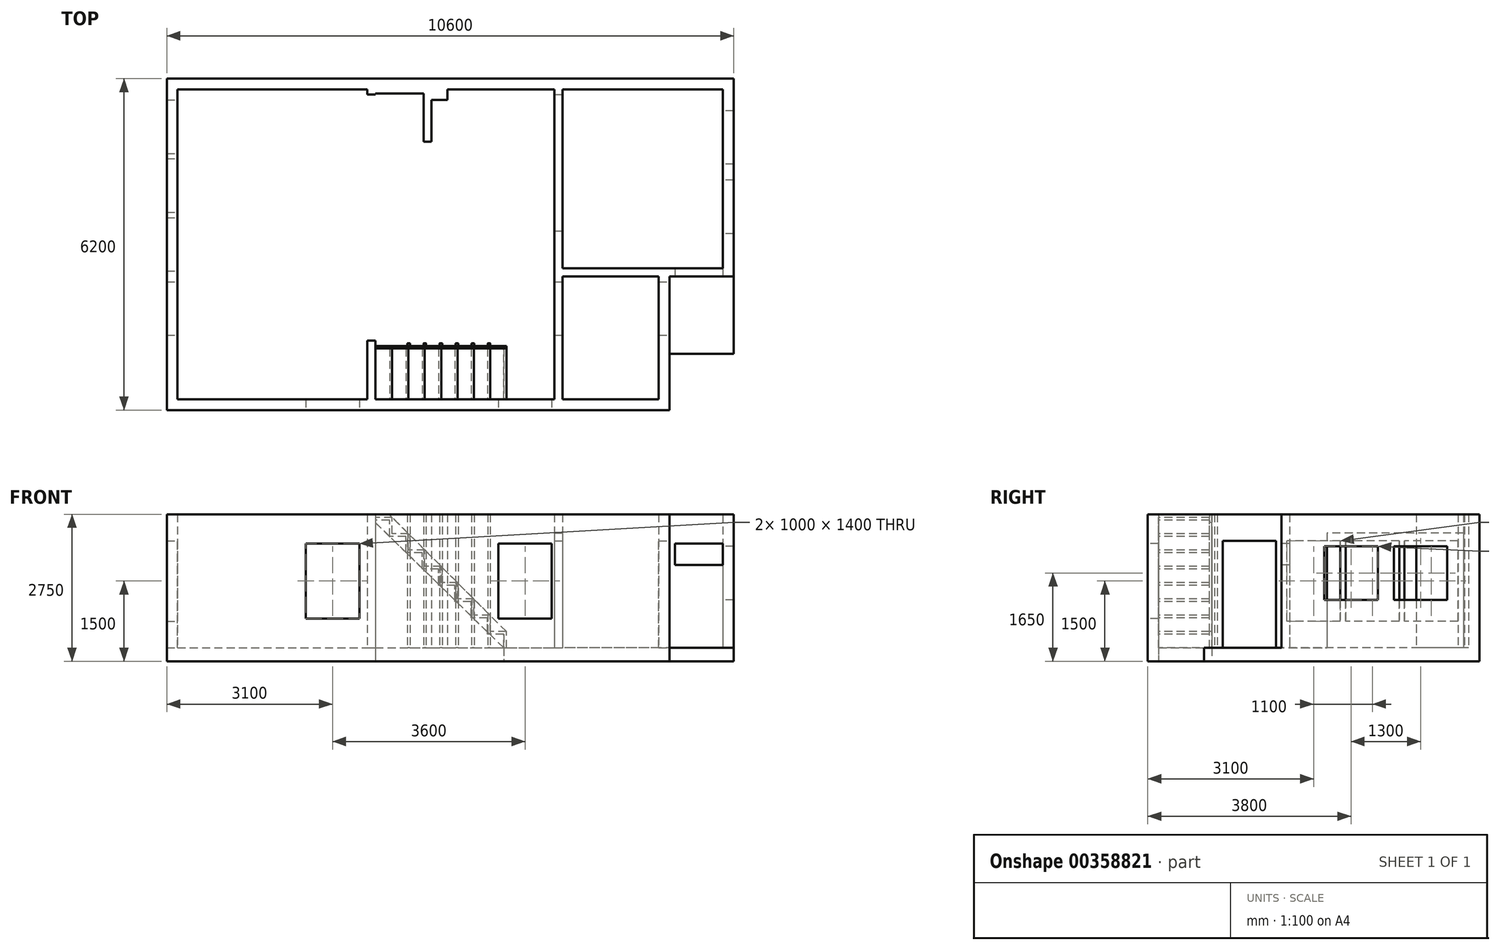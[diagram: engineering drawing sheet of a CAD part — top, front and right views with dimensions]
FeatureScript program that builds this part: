
annotation { "Feature Type Name" : "Feature", "Feature Type Description" : "" }
export const myFeature = defineFeature(function(context is Context, id is Id, definition is map)
    precondition{}
    {
        {
            var Q0;
            Q0=qCreatedBy(makeId("Top.planeOp"),FACE);
            var sketch = newSketch(context, id + "F0", { "sketchPlane" : qUnion([Q0])});
            skLineSegment(sketch, "E0.bottom", {"start": v(0, 0) * mm, "end": v(10600, 0) * mm});
            skLineSegment(sketch, "E0.top", {"start": v(0, -6200) * mm, "end": v(9400, -6200) * mm});
            skLineSegment(sketch, "E0.left", {"start": v(0, 0) * mm, "end": v(0, -6200) * mm});
            skLineSegment(sketch, "E0.right", {"start": v(10600, 0) * mm, "end": v(10600, -5150) * mm});
            skLineSegment(sketch, "E1.top", {"start": v(10600, -5150) * mm, "end": v(9400, -5150) * mm});
            skLineSegment(sketch, "E1.right", {"start": v(9400, -6200) * mm, "end": v(9400, -5150) * mm});
            skLineSegment(sketch, "E2.top", {"start": v(3900, -5000) * mm, "end": v(6300, -5000) * mm});
            skLineSegment(sketch, "E2.left", {"start": v(3900, -6000) * mm, "end": v(3900, -5000) * mm});
            skLineSegment(sketch, "E2.right", {"start": v(6300, -6000) * mm, "end": v(6300, -5000) * mm});
            skLineSegment(sketch, "E3.top", {"start": v(3900, -6000) * mm, "end": v(6300, -6000) * mm});
            skSolve(sketch);
        }
        {
            var Q0;
            Q0 = qSketchRegion(id + "F0", true);
            extrude(context, id + "F1", {"entities" : qUnion([Q0]), "depth" : 250 * mm});
        }
        {
            var Q0;
            Q0=makeQuery(id+"F1.opExtrude","CAP_FACE",FACE,{"disambiguationData":[OSD([sQuery(id+"F0.wireOp",EDGE,"E0.bottom"),sQuery(id+"F0.wireOp",EDGE,"E0.top"),sQuery(id+"F0.wireOp",EDGE,"E0.left"),sQuery(id+"F0.wireOp",EDGE,"E0.right")])],"isStart":false});
            var sketch = newSketch(context, id + "F2", { "sketchPlane" : qUnion([Q0])});
            skLineSegment(sketch, "E4.bottom", {"start": v(200, -200) * mm, "end": v(3750, -200) * mm});
            skLineSegment(sketch, "E4.top", {"start": v(200, -6000) * mm, "end": v(3750, -6000) * mm});
            skLineSegment(sketch, "E4.left", {"start": v(200, -200) * mm, "end": v(200, -6000) * mm});
            skLineSegment(sketch, "E4.right", {"start": v(10400, -200) * mm, "end": v(10400, -3550) * mm});
            skLineSegment(sketch, "E5.bottom", {"start": v(9200, -6000) * mm, "end": v(7400, -6000) * mm});
            skLineSegment(sketch, "E5.top", {"start": v(10400, -3550) * mm, "end": v(7400, -3550) * mm});
            skLineSegment(sketch, "E6.top", {"start": v(3750, -4900) * mm, "end": v(3900, -4900) * mm});
            skLineSegment(sketch, "E6.left", {"start": v(3750, -6000) * mm, "end": v(3750, -4900) * mm});
            skLineSegment(sketch, "E6.right", {"start": v(3900, -6000) * mm, "end": v(3900, -4900) * mm});
            skLineSegment(sketch, "E7.top", {"start": v(3750, -300) * mm, "end": v(3900, -300) * mm});
            skLineSegment(sketch, "E7.left", {"start": v(3750, -200) * mm, "end": v(3750, -300) * mm});
            skLineSegment(sketch, "E7.right", {"start": v(3900, -280) * mm, "end": v(3900, -300) * mm});
            skLineSegment(sketch, "E8.top", {"start": v(4800, -1180) * mm, "end": v(4950, -1180) * mm});
            skLineSegment(sketch, "E8.left", {"start": v(4800, -280) * mm, "end": v(4800, -1180) * mm});
            skLineSegment(sketch, "E8.right", {"start": v(4950, -400) * mm, "end": v(4950, -1180) * mm});
            skLineSegment(sketch, "E9.top", {"start": v(7250, -300) * mm, "end": v(7400, -300) * mm});
            skLineSegment(sketch, "E9.left", {"start": v(7250, -200) * mm, "end": v(7250, -300) * mm});
            skLineSegment(sketch, "E9.right", {"start": v(7400, -200) * mm, "end": v(7400, -300) * mm});
            skLineSegment(sketch, "E10.top", {"start": v(9200, -3700) * mm, "end": v(7400, -3700) * mm});
            skLineSegment(sketch, "E10.right", {"start": v(7400, -6000) * mm, "end": v(7400, -3700) * mm});
            skLineSegment(sketch, "E11.top", {"start": v(7250, -2850) * mm, "end": v(7400, -2850) * mm});
            skLineSegment(sketch, "E11.left", {"start": v(7250, -6000) * mm, "end": v(7250, -2850) * mm});
            skLineSegment(sketch, "E11.right", {"start": v(7400, -3550) * mm, "end": v(7400, -2850) * mm});
            skLineSegment(sketch, "E12.bottom", {"start": v(0, 0) * mm, "end": v(10600, 0) * mm});
            skLineSegment(sketch, "E12.top", {"start": v(0, -6200) * mm, "end": v(9400, -6200) * mm});
            skLineSegment(sketch, "E12.left", {"start": v(0, 0) * mm, "end": v(0, -6200) * mm});
            skLineSegment(sketch, "E12.right", {"start": v(10600, 0) * mm, "end": v(10600, -3700) * mm});
            skLineSegment(sketch, "E13.trimOffspring", {"start": v(5250, -200) * mm, "end": v(7250, -200) * mm});
            skLineSegment(sketch, "E14.trimOffspring", {"start": v(7400, -200) * mm, "end": v(10400, -200) * mm});
            skLineSegment(sketch, "E15.trimOffspring", {"start": v(3900, -6000) * mm, "end": v(7250, -6000) * mm});
            skLineSegment(sketch, "E16.top", {"start": v(4950, -400) * mm, "end": v(5250, -400) * mm});
            skLineSegment(sketch, "E16.right", {"start": v(5250, -200) * mm, "end": v(5250, -400) * mm});
            skLineSegment(sketch, "E17.top", {"start": v(3900, -280) * mm, "end": v(4800, -280) * mm});
            skLineSegment(sketch, "E18.trimOffspring", {"start": v(7400, -6000) * mm, "end": v(9200, -6000) * mm});
            skLineSegment(sketch, "E19.trimOffspring", {"start": v(9200, -3700) * mm, "end": v(9200, -6000) * mm});
            skLineSegment(sketch, "E20", {"start": v(10600, -3700) * mm, "end": v(9400, -3700) * mm});
            skLineSegment(sketch, "E21", {"start": v(9400, -3700) * mm, "end": v(9400, -6200) * mm});
            skSolve(sketch);
        }
        {
            var Q0;
            Q0 = qSketchRegion(id + "F2", true);
            extrude(context, id + "F3", {"entities" : qUnion([Q0]), "operationType" : NewBodyOperationType.ADD, "depth" : 2500 * mm});
        }
        {
            var Q0;
            Q0=makeQuery(id+"F3.boolean.opBoolean","MERGE",FACE,{"derivedFrom":[makeQuery(id+"F1.opExtrude","SWEPT_FACE",FACE,{"disambiguationData":[OSD([sQuery(id+"F0.wireOp",EDGE,"E1.right")])]}),makeQuery(id+"F3.opExtrude","SWEPT_FACE",FACE,{"disambiguationData":[OSD([sQuery(id+"F2.wireOp",EDGE,"E21")])]})]});
            var sketch = newSketch(context, id + "F4", { "sketchPlane" : qUnion([Q0])});
            skLineSegment(sketch, "E22.bottom", {"start": v(-4800, 250) * mm, "end": v(-3800, 250) * mm});
            skLineSegment(sketch, "E22.top", {"start": v(-4800, 2250) * mm, "end": v(-3800, 2250) * mm});
            skLineSegment(sketch, "E22.left", {"start": v(-4800, 250) * mm, "end": v(-4800, 2250) * mm});
            skLineSegment(sketch, "E22.right", {"start": v(-3800, 250) * mm, "end": v(-3800, 2250) * mm});
            skSolve(sketch);
        }
        {
            var Q0;
            Q0 = qSketchRegion(id + "F4", true);
            extrude(context, id + "F5", {"entities" : qUnion([Q0]), "operationType" : NewBodyOperationType.REMOVE, "endBound" : BoundingType.THROUGH_ALL, "oppositeDirection" : true, "depth" : 3000 * mm});
        }
        {
            var Q0;
            Q0=makeQuery(id+"F3.boolean.opBoolean","MERGE",FACE,{"derivedFrom":[makeQuery(id+"F1.opExtrude","SWEPT_FACE",FACE,{"disambiguationData":[OSD([sQuery(id+"F0.wireOp",EDGE,"E0.top")])]}),makeQuery(id+"F3.opExtrude","SWEPT_FACE",FACE,{"disambiguationData":[OSD([sQuery(id+"F2.wireOp",EDGE,"E12.top")])]})]});
            var sketch = newSketch(context, id + "F6", { "sketchPlane" : qUnion([Q0])});
            skLineSegment(sketch, "E23.bottom", {"start": v(7200, 2200) * mm, "end": v(6200, 2200) * mm});
            skLineSegment(sketch, "E23.top", {"start": v(7200, 800) * mm, "end": v(6200, 800) * mm});
            skLineSegment(sketch, "E23.left", {"start": v(7200, 2200) * mm, "end": v(7200, 800) * mm});
            skLineSegment(sketch, "E23.right", {"start": v(6200, 2200) * mm, "end": v(6200, 800) * mm});
            skLineSegment(sketch, "E24.bottom", {"start": v(2600, 2200) * mm, "end": v(3600, 2200) * mm});
            skLineSegment(sketch, "E24.top", {"start": v(2600, 800) * mm, "end": v(3600, 800) * mm});
            skLineSegment(sketch, "E24.left", {"start": v(2600, 2200) * mm, "end": v(2600, 800) * mm});
            skLineSegment(sketch, "E24.right", {"start": v(3600, 2200) * mm, "end": v(3600, 800) * mm});
            skLineSegment(sketch, "E25.bottom", {"start": v(9500, 2200) * mm, "end": v(10400, 2200) * mm});
            skLineSegment(sketch, "E25.top", {"start": v(9500, 1800) * mm, "end": v(10400, 1800) * mm});
            skLineSegment(sketch, "E25.left", {"start": v(9500, 2200) * mm, "end": v(9500, 1800) * mm});
            skLineSegment(sketch, "E25.right", {"start": v(10400, 2200) * mm, "end": v(10400, 1800) * mm});
            skSolve(sketch);
        }
        {
            var Q0;
            Q0 = qSketchRegion(id + "F6", true);
            var Q1;
            Q1=makeQuery(id+"F3.opExtrude","SWEPT_FACE",FACE,{"disambiguationData":[OSD([sQuery(id+"F2.wireOp",EDGE,"E4.bottom")])]});
            extrude(context, id + "F7", {"entities" : qUnion([Q0]), "operationType" : NewBodyOperationType.REMOVE, "endBound" : BoundingType.UP_TO_SURFACE, "oppositeDirection" : true, "endBoundEntityFace" : qUnion([Q1]), "depth" : 25 * mm});
        }
        {
            var Q0;
            Q0=makeQuery(id+"F3.opExtrude","SWEPT_FACE",FACE,{"disambiguationData":[OSD([sQuery(id+"F2.wireOp",EDGE,"E4.right")])]});
            var sketch = newSketch(context, id + "F8", { "sketchPlane" : qUnion([Q0])});
            skLineSegment(sketch, "E26.bottom", {"start": v(600, 2150) * mm, "end": v(1600, 2150) * mm});
            skLineSegment(sketch, "E26.top", {"start": v(600, 1150) * mm, "end": v(1600, 1150) * mm});
            skLineSegment(sketch, "E26.left", {"start": v(600, 2150) * mm, "end": v(600, 1150) * mm});
            skLineSegment(sketch, "E26.right", {"start": v(1600, 2150) * mm, "end": v(1600, 1150) * mm});
            skLineSegment(sketch, "E27.bottom", {"start": v(1900, 2150) * mm, "end": v(2900, 2150) * mm});
            skLineSegment(sketch, "E27.top", {"start": v(1900, 1150) * mm, "end": v(2900, 1150) * mm});
            skLineSegment(sketch, "E27.left", {"start": v(1900, 2150) * mm, "end": v(1900, 1150) * mm});
            skLineSegment(sketch, "E27.right", {"start": v(2900, 2150) * mm, "end": v(2900, 1150) * mm});
            skSolve(sketch);
        }
        {
            var Q0;
            Q0 = qSketchRegion(id + "F8", true);
            extrude(context, id + "F9", {"entities" : qUnion([Q0]), "operationType" : NewBodyOperationType.REMOVE, "endBound" : BoundingType.UP_TO_NEXT, "oppositeDirection" : true, "depth" : 25 * mm});
        }
        {
            var Q0;
            Q0=makeQuery(id+"F3.opExtrude","SWEPT_FACE",FACE,{"disambiguationData":[OSD([sQuery(id+"F2.wireOp",EDGE,"E4.left")])]});
            var sketch = newSketch(context, id + "F10", { "sketchPlane" : qUnion([Q0])});
            skLineSegment(sketch, "E28.bottom", {"start": v(-3600, 2250) * mm, "end": v(-2600, 2250) * mm});
            skLineSegment(sketch, "E28.top", {"start": v(-3600, 750) * mm, "end": v(-2600, 750) * mm});
            skLineSegment(sketch, "E28.left", {"start": v(-3600, 2250) * mm, "end": v(-3600, 750) * mm});
            skLineSegment(sketch, "E28.right", {"start": v(-2600, 2250) * mm, "end": v(-2600, 750) * mm});
            skLineSegment(sketch, "E29.bottom", {"start": v(-2500, 2250) * mm, "end": v(-1500, 2250) * mm});
            skLineSegment(sketch, "E29.top", {"start": v(-2500, 750) * mm, "end": v(-1500, 750) * mm});
            skLineSegment(sketch, "E29.left", {"start": v(-2500, 2250) * mm, "end": v(-2500, 750) * mm});
            skLineSegment(sketch, "E29.right", {"start": v(-1500, 2250) * mm, "end": v(-1500, 750) * mm});
            skLineSegment(sketch, "E30.bottom", {"start": v(-1400, 2250) * mm, "end": v(-400, 2250) * mm});
            skLineSegment(sketch, "E30.top", {"start": v(-1400, 750) * mm, "end": v(-400, 750) * mm});
            skLineSegment(sketch, "E30.left", {"start": v(-1400, 2250) * mm, "end": v(-1400, 750) * mm});
            skLineSegment(sketch, "E30.right", {"start": v(-400, 2250) * mm, "end": v(-400, 750) * mm});
            skSolve(sketch);
        }
        {
            var Q0;
            Q0 = qSketchRegion(id + "F10", true);
            extrude(context, id + "F11", {"entities" : qUnion([Q0]), "operationType" : NewBodyOperationType.REMOVE, "endBound" : BoundingType.UP_TO_NEXT, "oppositeDirection" : true, "depth" : 25 * mm});
        }
        {
            var Q0;
            Q0=makeQuery(id+"F3.opExtrude","CAP_FACE",FACE,{"disambiguationData":[OSD([sQuery(id+"F2.wireOp",EDGE,"E4.bottom"),sQuery(id+"F2.wireOp",EDGE,"E4.top"),sQuery(id+"F2.wireOp",EDGE,"E4.left"),sQuery(id+"F2.wireOp",EDGE,"E4.right"),sQuery(id+"F2.wireOp",EDGE,"E5.top"),sQuery(id+"F2.wireOp",EDGE,"E6.top"),sQuery(id+"F2.wireOp",EDGE,"E6.left"),sQuery(id+"F2.wireOp",EDGE,"E6.right"),sQuery(id+"F2.wireOp",EDGE,"E7.top"),sQuery(id+"F2.wireOp",EDGE,"E7.left"),sQuery(id+"F2.wireOp",EDGE,"E7.right"),sQuery(id+"F2.wireOp",EDGE,"E8.top"),sQuery(id+"F2.wireOp",EDGE,"E8.left"),sQuery(id+"F2.wireOp",EDGE,"E8.right"),sQuery(id+"F2.wireOp",EDGE,"E9.top"),sQuery(id+"F2.wireOp",EDGE,"E9.left"),sQuery(id+"F2.wireOp",EDGE,"E9.right"),sQuery(id+"F2.wireOp",EDGE,"E10.top"),sQuery(id+"F2.wireOp",EDGE,"E10.right"),sQuery(id+"F2.wireOp",EDGE,"E11.top"),sQuery(id+"F2.wireOp",EDGE,"E11.left"),sQuery(id+"F2.wireOp",EDGE,"E11.right"),sQuery(id+"F2.wireOp",EDGE,"E12.bottom"),sQuery(id+"F2.wireOp",EDGE,"E12.top"),sQuery(id+"F2.wireOp",EDGE,"E12.left"),sQuery(id+"F2.wireOp",EDGE,"E12.right"),sQuery(id+"F2.wireOp",EDGE,"E13.trimOffspring"),sQuery(id+"F2.wireOp",EDGE,"E14.trimOffspring"),sQuery(id+"F2.wireOp",EDGE,"E15.trimOffspring"),sQuery(id+"F2.wireOp",EDGE,"E16.top"),sQuery(id+"F2.wireOp",EDGE,"E16.right"),sQuery(id+"F2.wireOp",EDGE,"E17.top"),sQuery(id+"F2.wireOp",EDGE,"E18.trimOffspring"),sQuery(id+"F2.wireOp",EDGE,"E19.trimOffspring"),sQuery(id+"F2.wireOp",EDGE,"E20"),sQuery(id+"F2.wireOp",EDGE,"E21")])],"isStart":false});
            var sketch = newSketch(context, id + "F12", { "sketchPlane" : qUnion([Q0])});
            skLineSegment(sketch, "E31.bottom", {"start": v(7250, -300) * mm, "end": v(7400, -300) * mm});
            skLineSegment(sketch, "E31.top", {"start": v(7250, -2850) * mm, "end": v(7400, -2850) * mm});
            skLineSegment(sketch, "E31.left", {"start": v(7250, -300) * mm, "end": v(7250, -2850) * mm});
            skLineSegment(sketch, "E31.right", {"start": v(7400, -300) * mm, "end": v(7400, -2850) * mm});
            skSolve(sketch);
        }
        {
            var Q0;
            Q0 = qSketchRegion(id + "F12", true);
            extrude(context, id + "F13", {"entities" : qUnion([Q0]), "operationType" : NewBodyOperationType.ADD, "oppositeDirection" : true, "depth" : 350 * mm});
        }
        {
            var Q0;
            Q0=makeQuery(id+"F3.boolean.opBoolean","MERGE",FACE,{"derivedFrom":[makeQuery(id+"F1.opExtrude","SWEPT_FACE",FACE,{"disambiguationData":[OSD([sQuery(id+"F0.wireOp",EDGE,"E3.top")])]}),makeQuery(id+"F3.opExtrude","SWEPT_FACE",FACE,{"disambiguationData":[OSD([sQuery(id+"F2.wireOp",EDGE,"E15.trimOffspring")])]})]});
            var sketch = newSketch(context, id + "F14", { "sketchPlane" : qUnion([Q0])});
            skLineSegment(sketch, "E32", {"start": v(-6350, 250) * mm, "end": v(-6350, 555) * mm});
            skLineSegment(sketch, "E33", {"start": v(-6350, 555) * mm, "end": v(-6045, 555) * mm});
            skLineSegment(sketch, "E34", {"start": v(-6045, 555) * mm, "end": v(-6045, 860) * mm});
            skLineSegment(sketch, "E35", {"start": v(-6045, 860) * mm, "end": v(-5740, 860) * mm});
            skLineSegment(sketch, "E36", {"start": v(-5740, 860) * mm, "end": v(-5740, 1165) * mm});
            skLineSegment(sketch, "E37", {"start": v(-5740, 1165) * mm, "end": v(-5435, 1165) * mm});
            skLineSegment(sketch, "E38", {"start": v(-5435, 1165) * mm, "end": v(-5435, 1470) * mm});
            skLineSegment(sketch, "E39", {"start": v(-5435, 1470) * mm, "end": v(-5130, 1470) * mm});
            skLineSegment(sketch, "E40", {"start": v(-5130, 1470) * mm, "end": v(-5130, 1775) * mm});
            skLineSegment(sketch, "E41", {"start": v(-5130, 1775) * mm, "end": v(-4825, 1775) * mm});
            skLineSegment(sketch, "E42", {"start": v(-4825, 1775) * mm, "end": v(-4825, 2080) * mm});
            skLineSegment(sketch, "E43", {"start": v(-4825, 2080) * mm, "end": v(-4520, 2080) * mm});
            skLineSegment(sketch, "E44", {"start": v(-4520, 2080) * mm, "end": v(-4520, 2385) * mm});
            skLineSegment(sketch, "E45", {"start": v(-4520, 2385) * mm, "end": v(-4215, 2385) * mm});
            skLineSegment(sketch, "E46", {"start": v(-4215, 2385) * mm, "end": v(-4215, 2690) * mm});
            skLineSegment(sketch, "E47", {"start": v(-4215, 2690) * mm, "end": v(-3900, 2690) * mm});
            skLineSegment(sketch, "E48.0", {"start": v(-4165, 2640) * mm, "end": v(-3900, 2640) * mm});
            skLineSegment(sketch, "E48.1", {"start": v(-4165, 2335) * mm, "end": v(-4165, 2640) * mm});
            skLineSegment(sketch, "E48.2", {"start": v(-4470, 2335) * mm, "end": v(-4165, 2335) * mm});
            skLineSegment(sketch, "E48.3", {"start": v(-4470, 2030) * mm, "end": v(-4470, 2335) * mm});
            skLineSegment(sketch, "E48.4", {"start": v(-4775, 2030) * mm, "end": v(-4470, 2030) * mm});
            skLineSegment(sketch, "E48.5", {"start": v(-4775, 1725) * mm, "end": v(-4775, 2030) * mm});
            skLineSegment(sketch, "E48.6", {"start": v(-5995, 810) * mm, "end": v(-5690, 810) * mm});
            skLineSegment(sketch, "E48.7", {"start": v(-5995, 505) * mm, "end": v(-5995, 810) * mm});
            skLineSegment(sketch, "E48.8", {"start": v(-6300, 505) * mm, "end": v(-5995, 505) * mm});
            skLineSegment(sketch, "E48.9", {"start": v(-6300, 250) * mm, "end": v(-6300, 505) * mm});
            skLineSegment(sketch, "E48.10", {"start": v(-5690, 810) * mm, "end": v(-5690, 1115) * mm});
            skLineSegment(sketch, "E48.11", {"start": v(-5690, 1115) * mm, "end": v(-5385, 1115) * mm});
            skLineSegment(sketch, "E48.12", {"start": v(-5385, 1115) * mm, "end": v(-5385, 1420) * mm});
            skLineSegment(sketch, "E48.13", {"start": v(-5385, 1420) * mm, "end": v(-5080, 1420) * mm});
            skLineSegment(sketch, "E48.14", {"start": v(-5080, 1420) * mm, "end": v(-5080, 1725) * mm});
            skLineSegment(sketch, "E48.15", {"start": v(-5080, 1725) * mm, "end": v(-4775, 1725) * mm});
            skLineSegment(sketch, "E49", {"start": v(-3900, 2690) * mm, "end": v(-3900, 2640) * mm});
            skLineSegment(sketch, "E50", {"start": v(-6350, 250) * mm, "end": v(-6300, 250) * mm});
            skSolve(sketch);
        }
        {
            var Q0;
            Q0 = qSketchRegion(id + "F14", true);
            extrude(context, id + "F15", {"entities" : qUnion([Q0]), "operationType" : NewBodyOperationType.ADD, "depth" : 950 * mm});
        }
        {
            var Q0;
            Q0=makeQuery(id+"F15.opExtrude","CAP_FACE",FACE,{"disambiguationData":[OSD([sQuery(id+"F14.wireOp",EDGE,"E32"),sQuery(id+"F14.wireOp",EDGE,"E33"),sQuery(id+"F14.wireOp",EDGE,"E34"),sQuery(id+"F14.wireOp",EDGE,"E35"),sQuery(id+"F14.wireOp",EDGE,"E36"),sQuery(id+"F14.wireOp",EDGE,"E37"),sQuery(id+"F14.wireOp",EDGE,"E38"),sQuery(id+"F14.wireOp",EDGE,"E39"),sQuery(id+"F14.wireOp",EDGE,"E40"),sQuery(id+"F14.wireOp",EDGE,"E41"),sQuery(id+"F14.wireOp",EDGE,"E42"),sQuery(id+"F14.wireOp",EDGE,"E43"),sQuery(id+"F14.wireOp",EDGE,"E44"),sQuery(id+"F14.wireOp",EDGE,"E45"),sQuery(id+"F14.wireOp",EDGE,"E46"),sQuery(id+"F14.wireOp",EDGE,"E47"),sQuery(id+"F14.wireOp",EDGE,"E48.0"),sQuery(id+"F14.wireOp",EDGE,"E48.1"),sQuery(id+"F14.wireOp",EDGE,"E48.2"),sQuery(id+"F14.wireOp",EDGE,"E48.3"),sQuery(id+"F14.wireOp",EDGE,"E48.4"),sQuery(id+"F14.wireOp",EDGE,"E48.5"),sQuery(id+"F14.wireOp",EDGE,"E48.6"),sQuery(id+"F14.wireOp",EDGE,"E48.7"),sQuery(id+"F14.wireOp",EDGE,"E48.8"),sQuery(id+"F14.wireOp",EDGE,"E48.9"),sQuery(id+"F14.wireOp",EDGE,"E48.10"),sQuery(id+"F14.wireOp",EDGE,"E48.11"),sQuery(id+"F14.wireOp",EDGE,"E48.12"),sQuery(id+"F14.wireOp",EDGE,"E48.13"),sQuery(id+"F14.wireOp",EDGE,"E48.14"),sQuery(id+"F14.wireOp",EDGE,"E48.15"),sQuery(id+"F14.wireOp",EDGE,"E49"),sQuery(id+"F14.wireOp",EDGE,"E50")])],"isStart":false});
            var sketch = newSketch(context, id + "F16", { "sketchPlane" : qUnion([Q0])});
            skLineSegment(sketch, "E51", {"start": v(-6350, 555) * mm, "end": v(-4156.2, 2748.8) * mm});
            skLineSegment(sketch, "E52", {"start": v(-4215, 2690) * mm, "end": v(-3900, 2690) * mm, "construction": true});
            skLineSegment(sketch, "E53", {"start": v(-3900, 2748.8) * mm, "end": v(-3900, 2593.8) * mm});
            skLineSegment(sketch, "E54", {"start": v(-6300, 250) * mm, "end": v(-4165, 2335) * mm});
            skLineSegment(sketch, "E55", {"start": v(-4165, 2335) * mm, "end": v(-3900, 2593.8) * mm});
            skLineSegment(sketch, "E56", {"start": v(-6350, 555) * mm, "end": v(-6350, 250) * mm});
            skLineSegment(sketch, "E57", {"start": v(-6350, 250) * mm, "end": v(-6300, 250) * mm});
            skLineSegment(sketch, "E58", {"start": v(-4156.2, 2748.8) * mm, "end": v(-3900, 2748.8) * mm});
            skSolve(sketch);
        }
        {
            var Q0;
            Q0 = qSketchRegion(id + "F16", true);
            extrude(context, id + "F17", {"entities" : qUnion([Q0]), "operationType" : NewBodyOperationType.ADD, "depth" : 50 * mm});
        }
        {
            var Q0;
            {var subQ0=sQuery(id+"F0.wireOp",EDGE,"E3.top");var subQ1=sQuery(id+"F0.wireOp",EDGE,"E2.right");var subQ2=sQuery(id+"F0.wireOp",EDGE,"E2.left");var subQ3=sQuery(id+"F0.wireOp",EDGE,"E2.top");var subQ4=sQuery(id+"F0.wireOp",EDGE,"E1.right");var subQ5=sQuery(id+"F0.wireOp",EDGE,"E1.top");var subQ6=sQuery(id+"F0.wireOp",EDGE,"E0.right");var subQ7=makeQuery(id+"F1.opExtrude","CAP_FACE",FACE,{"disambiguationData":[OSD([sQuery(id+"F0.wireOp",EDGE,"E0.bottom"),sQuery(id+"F0.wireOp",EDGE,"E0.top"),sQuery(id+"F0.wireOp",EDGE,"E0.left"),subQ6,subQ5,subQ4,subQ3,subQ2,subQ1,subQ0])],"isStart":false});Q0=makeQuery(id+"F5.boolean.opBoolean","MERGE",FACE,{"derivedFrom":[makeQuery(id+"F3.boolean.opBoolean","SPLIT",FACE,{"disambiguationData":[TD([makeQuery(id+"F1.opExtrude","SWEPT_FACE",FACE,{"disambiguationData":[OSD([subQ6])]})])],"derivedFrom":subQ7}),makeQuery(id+"F3.boolean.opBoolean","SPLIT",FACE,{"disambiguationData":[TD([makeQuery(id+"F1.opExtrude","SWEPT_FACE",FACE,{"disambiguationData":[OSD([subQ3])]})])],"derivedFrom":subQ7}),makeQuery(id+"F3.boolean.opBoolean","SPLIT",FACE,{"disambiguationData":[TD([makeQuery(id+"F3.opExtrude","SWEPT_FACE",FACE,{"disambiguationData":[OSD([sQuery(id+"F2.wireOp",EDGE,"E10.top")])]})])],"derivedFrom":subQ7}),makeQuery(id+"F5.opExtrude","SWEPT_FACE",FACE,{"disambiguationData":[OSD([sQuery(id+"F4.wireOp",EDGE,"E22.bottom")])]})]});}
            var sketch = newSketch(context, id + "F18", { "sketchPlane" : qUnion([Q0])});
            skLineSegment(sketch, "E59.bottom", {"start": v(6045, -5000) * mm, "end": v(6005, -5000) * mm});
            skLineSegment(sketch, "E59.top", {"start": v(6045, -4950) * mm, "end": v(6005, -4950) * mm});
            skLineSegment(sketch, "E59.left", {"start": v(6050, -4995) * mm, "end": v(6050, -4955) * mm});
            skLineSegment(sketch, "E59.right", {"start": v(6000, -4995) * mm, "end": v(6000, -4955) * mm});
            skPoint(sketch, "E60.visualSharp", {"position": v(6000, -4950) * mm});
            skArc(sketch, "E60.filletArc", {"start": v(6005, -4950) * mm, "mid": v(6001.46, -4951.46) * mm, "end": v(6000, -4955) * mm});
            skPoint(sketch, "E61.visualSharp", {"position": v(6050, -4950) * mm});
            skArc(sketch, "E61.filletArc", {"start": v(6050, -4955) * mm, "mid": v(6048.54, -4951.46) * mm, "end": v(6045, -4950) * mm});
            skPoint(sketch, "E62.visualSharp", {"position": v(6050, -5000) * mm});
            skArc(sketch, "E62.filletArc", {"start": v(6045, -5000) * mm, "mid": v(6048.54, -4998.54) * mm, "end": v(6050, -4995) * mm});
            skPoint(sketch, "E63.visualSharp", {"position": v(6000, -5000) * mm});
            skArc(sketch, "E63.filletArc", {"start": v(6000, -4995) * mm, "mid": v(6001.46, -4998.54) * mm, "end": v(6005, -5000) * mm});
            skPoint(sketch, "E64.1.0.0", {"position": v(5700, -5000) * mm});
            skLineSegment(sketch, "E64.1.0.1", {"start": v(5745, -5000) * mm, "end": v(5705, -5000) * mm});
            skLineSegment(sketch, "E64.1.0.2", {"start": v(5745, -4950) * mm, "end": v(5705, -4950) * mm});
            skPoint(sketch, "E64.1.0.3", {"position": v(5700, -4950) * mm});
            skLineSegment(sketch, "E64.1.0.4", {"start": v(5750, -4995) * mm, "end": v(5750, -4955) * mm});
            skPoint(sketch, "E64.1.0.5", {"position": v(5750, -4950) * mm});
            skPoint(sketch, "E64.1.0.6", {"position": v(5750, -5000) * mm});
            skLineSegment(sketch, "E64.1.0.7", {"start": v(5700, -4995) * mm, "end": v(5700, -4955) * mm});
            skArc(sketch, "E64.1.0.8", {"start": v(5750, -4955) * mm, "mid": v(5748.54, -4951.46) * mm, "end": v(5745, -4950) * mm});
            skArc(sketch, "E64.1.0.9", {"start": v(5705, -4950) * mm, "mid": v(5701.46, -4951.46) * mm, "end": v(5700, -4955) * mm});
            skArc(sketch, "E64.1.0.10", {"start": v(5700, -4995) * mm, "mid": v(5701.46, -4998.54) * mm, "end": v(5705, -5000) * mm});
            skArc(sketch, "E64.1.0.11", {"start": v(5745, -5000) * mm, "mid": v(5748.54, -4998.54) * mm, "end": v(5750, -4995) * mm});
            skPoint(sketch, "E64.2.0.0", {"position": v(5400, -5000) * mm});
            skLineSegment(sketch, "E64.2.0.1", {"start": v(5445, -5000) * mm, "end": v(5405, -5000) * mm});
            skLineSegment(sketch, "E64.2.0.2", {"start": v(5445, -4950) * mm, "end": v(5405, -4950) * mm});
            skPoint(sketch, "E64.2.0.3", {"position": v(5400, -4950) * mm});
            skLineSegment(sketch, "E64.2.0.4", {"start": v(5450, -4995) * mm, "end": v(5450, -4955) * mm});
            skPoint(sketch, "E64.2.0.5", {"position": v(5450, -4950) * mm});
            skPoint(sketch, "E64.2.0.6", {"position": v(5450, -5000) * mm});
            skLineSegment(sketch, "E64.2.0.7", {"start": v(5400, -4995) * mm, "end": v(5400, -4955) * mm});
            skArc(sketch, "E64.2.0.8", {"start": v(5450, -4955) * mm, "mid": v(5448.54, -4951.46) * mm, "end": v(5445, -4950) * mm});
            skArc(sketch, "E64.2.0.9", {"start": v(5405, -4950) * mm, "mid": v(5401.46, -4951.46) * mm, "end": v(5400, -4955) * mm});
            skArc(sketch, "E64.2.0.10", {"start": v(5400, -4995) * mm, "mid": v(5401.46, -4998.54) * mm, "end": v(5405, -5000) * mm});
            skArc(sketch, "E64.2.0.11", {"start": v(5445, -5000) * mm, "mid": v(5448.54, -4998.54) * mm, "end": v(5450, -4995) * mm});
            skPoint(sketch, "E64.3.0.0", {"position": v(5100, -5000) * mm});
            skLineSegment(sketch, "E64.3.0.1", {"start": v(5145, -5000) * mm, "end": v(5105, -5000) * mm});
            skLineSegment(sketch, "E64.3.0.2", {"start": v(5145, -4950) * mm, "end": v(5105, -4950) * mm});
            skPoint(sketch, "E64.3.0.3", {"position": v(5100, -4950) * mm});
            skLineSegment(sketch, "E64.3.0.4", {"start": v(5150, -4995) * mm, "end": v(5150, -4955) * mm});
            skPoint(sketch, "E64.3.0.5", {"position": v(5150, -4950) * mm});
            skPoint(sketch, "E64.3.0.6", {"position": v(5150, -5000) * mm});
            skLineSegment(sketch, "E64.3.0.7", {"start": v(5100, -4995) * mm, "end": v(5100, -4955) * mm});
            skArc(sketch, "E64.3.0.8", {"start": v(5150, -4955) * mm, "mid": v(5148.54, -4951.46) * mm, "end": v(5145, -4950) * mm});
            skArc(sketch, "E64.3.0.9", {"start": v(5105, -4950) * mm, "mid": v(5101.46, -4951.46) * mm, "end": v(5100, -4955) * mm});
            skArc(sketch, "E64.3.0.10", {"start": v(5100, -4995) * mm, "mid": v(5101.46, -4998.54) * mm, "end": v(5105, -5000) * mm});
            skArc(sketch, "E64.3.0.11", {"start": v(5145, -5000) * mm, "mid": v(5148.54, -4998.54) * mm, "end": v(5150, -4995) * mm});
            skPoint(sketch, "E64.4.0.0", {"position": v(4800, -5000) * mm});
            skLineSegment(sketch, "E64.4.0.1", {"start": v(4845, -5000) * mm, "end": v(4805, -5000) * mm});
            skLineSegment(sketch, "E64.4.0.2", {"start": v(4845, -4950) * mm, "end": v(4805, -4950) * mm});
            skPoint(sketch, "E64.4.0.3", {"position": v(4800, -4950) * mm});
            skLineSegment(sketch, "E64.4.0.4", {"start": v(4850, -4995) * mm, "end": v(4850, -4955) * mm});
            skPoint(sketch, "E64.4.0.5", {"position": v(4850, -4950) * mm});
            skPoint(sketch, "E64.4.0.6", {"position": v(4850, -5000) * mm});
            skLineSegment(sketch, "E64.4.0.7", {"start": v(4800, -4995) * mm, "end": v(4800, -4955) * mm});
            skArc(sketch, "E64.4.0.8", {"start": v(4850, -4955) * mm, "mid": v(4848.54, -4951.46) * mm, "end": v(4845, -4950) * mm});
            skArc(sketch, "E64.4.0.9", {"start": v(4805, -4950) * mm, "mid": v(4801.46, -4951.46) * mm, "end": v(4800, -4955) * mm});
            skArc(sketch, "E64.4.0.10", {"start": v(4800, -4995) * mm, "mid": v(4801.46, -4998.54) * mm, "end": v(4805, -5000) * mm});
            skArc(sketch, "E64.4.0.11", {"start": v(4845, -5000) * mm, "mid": v(4848.54, -4998.54) * mm, "end": v(4850, -4995) * mm});
            skPoint(sketch, "E64.5.0.0", {"position": v(4500, -5000) * mm});
            skLineSegment(sketch, "E64.5.0.1", {"start": v(4545, -5000) * mm, "end": v(4505, -5000) * mm});
            skLineSegment(sketch, "E64.5.0.2", {"start": v(4545, -4950) * mm, "end": v(4505, -4950) * mm});
            skPoint(sketch, "E64.5.0.3", {"position": v(4500, -4950) * mm});
            skLineSegment(sketch, "E64.5.0.4", {"start": v(4550, -4995) * mm, "end": v(4550, -4955) * mm});
            skPoint(sketch, "E64.5.0.5", {"position": v(4550, -4950) * mm});
            skPoint(sketch, "E64.5.0.6", {"position": v(4550, -5000) * mm});
            skLineSegment(sketch, "E64.5.0.7", {"start": v(4500, -4995) * mm, "end": v(4500, -4955) * mm});
            skArc(sketch, "E64.5.0.8", {"start": v(4550, -4955) * mm, "mid": v(4548.54, -4951.46) * mm, "end": v(4545, -4950) * mm});
            skArc(sketch, "E64.5.0.9", {"start": v(4505, -4950) * mm, "mid": v(4501.46, -4951.46) * mm, "end": v(4500, -4955) * mm});
            skArc(sketch, "E64.5.0.10", {"start": v(4500, -4995) * mm, "mid": v(4501.46, -4998.54) * mm, "end": v(4505, -5000) * mm});
            skArc(sketch, "E64.5.0.11", {"start": v(4545, -5000) * mm, "mid": v(4548.54, -4998.54) * mm, "end": v(4550, -4995) * mm});
            skLineSegment(sketch, "E64.direction1", {"start": v(6000, -5000) * mm, "end": v(5700, -5000) * mm, "construction": true});
            skSolve(sketch);
        }
        {
            var Q0;
            Q0 = qSketchRegion(id + "F18", true);
            extrude(context, id + "F19", {"entities" : qUnion([Q0]), "operationType" : NewBodyOperationType.ADD, "depth" : 2500 * mm});
        }
    });
